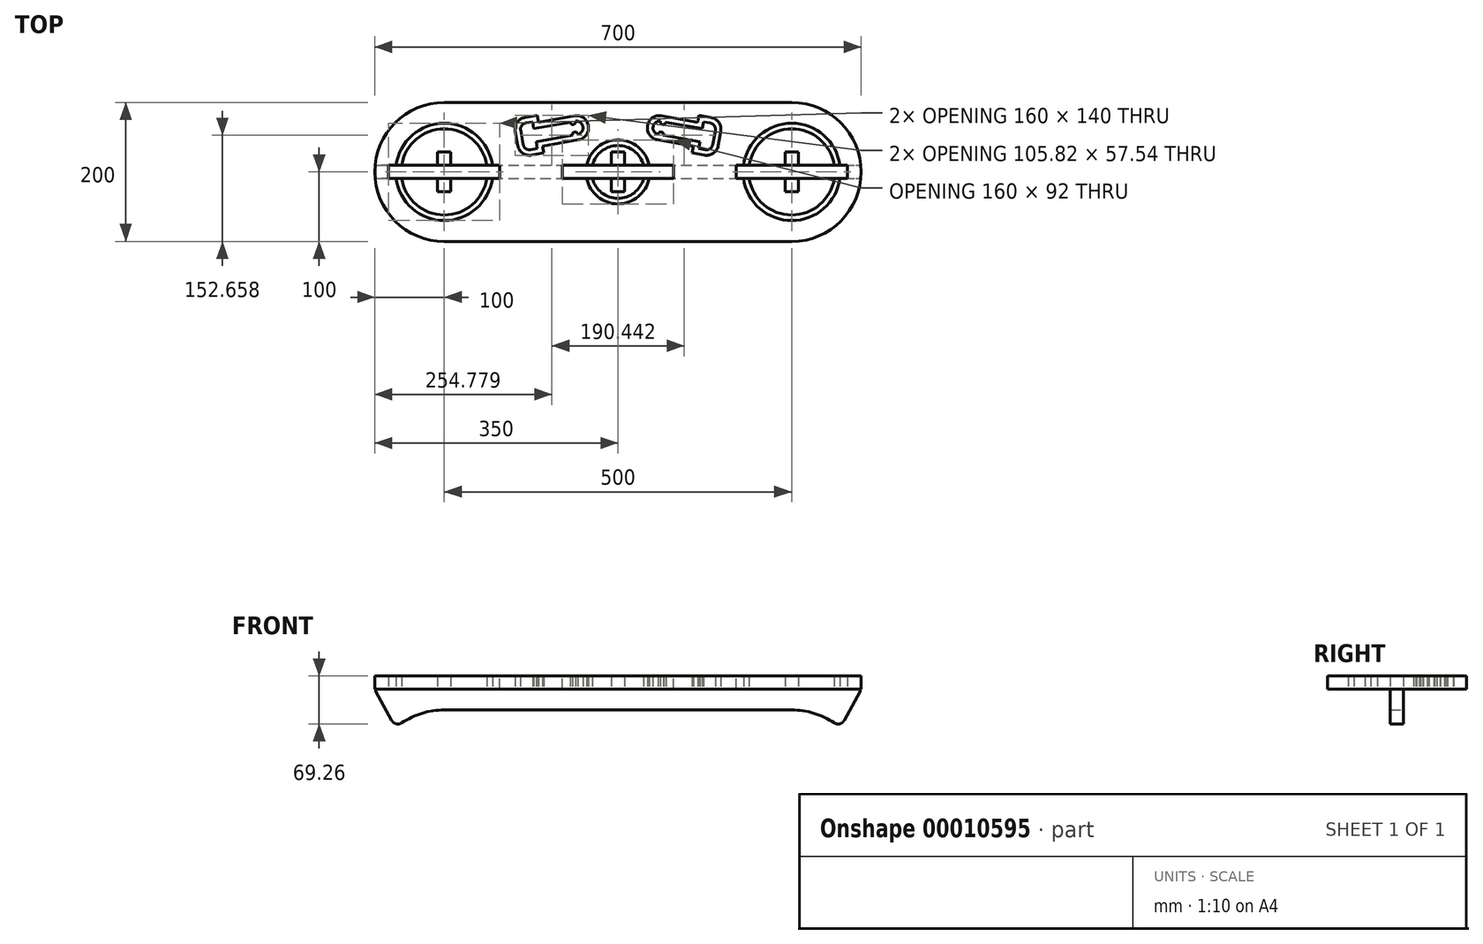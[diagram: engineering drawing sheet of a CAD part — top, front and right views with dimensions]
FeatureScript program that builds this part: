
annotation { "Feature Type Name" : "Feature", "Feature Type Description" : "" }
export const myFeature = defineFeature(function(context is Context, id is Id, definition is map)
    precondition{}
    {
        {
            var Q0;
            Q0=qCreatedBy(makeId("Top.planeOp"),FACE);
            var sketch = newSketch(context, id + "F0", { "sketchPlane" : qUnion([Q0])});
            skLineSegment(sketch, "E0.bottom", {"start": v(-250, 100) * mm, "end": v(250, 100) * mm});
            skLineSegment(sketch, "E0.top", {"start": v(-250, -100) * mm, "end": v(250, -100) * mm});
            skLineSegment(sketch, "E0.left", {"start": v(-250, 100) * mm, "end": v(-250, -100) * mm});
            skLineSegment(sketch, "E0.right", {"start": v(250, 100) * mm, "end": v(250, -100) * mm});
            skLineSegment(sketch, "E1", {"start": v(0, 0) * mm, "end": v(0, 100) * mm, "construction": true});
            skLineSegment(sketch, "E2", {"start": v(250, 0) * mm, "end": v(0, 0) * mm, "construction": true});
            skArc(sketch, "E3", {"start": v(-250, 100) * mm, "mid": v(-350, 0) * mm, "end": v(-250, -100) * mm});
            skArc(sketch, "E4", {"start": v(250, -100) * mm, "mid": v(350, 0) * mm, "end": v(250, 100) * mm});
            skSolve(sketch);
        }
        {
            var Q0;
            Q0=qSketchRegion(id+"F0",true);
            extrude(context, id + "F1", {"entities" : qUnion([Q0]), "depth" : 19 * mm});
        }
        {
            var Q0;
            Q0=qCreatedBy(makeId("Front.planeOp"),FACE);
            var sketch = newSketch(context, id + "F2", { "sketchPlane" : qUnion([Q0])});
            skLineSegment(sketch, "E5.top", {"start": v(-250, -30) * mm, "end": v(0, -30) * mm});
            skLineSegment(sketch, "E6", {"start": v(0, -30) * mm, "end": v(0, 0) * mm, "construction": true});
            skLineSegment(sketch, "E7.top", {"start": v(-330, 19) * mm, "end": v(-170, 19) * mm});
            skLineSegment(sketch, "E7.right", {"start": v(-170, 0) * mm, "end": v(-170, 19) * mm});
            skLineSegment(sketch, "E8.bottom", {"start": v(-80, 0) * mm, "end": v(80, 0) * mm});
            skLineSegment(sketch, "E8.top", {"start": v(-80, 19) * mm, "end": v(80, 19) * mm});
            skLineSegment(sketch, "E8.left", {"start": v(-80, 0) * mm, "end": v(-80, 19) * mm});
            skLineSegment(sketch, "E8.right", {"start": v(80, 0) * mm, "end": v(80, 19) * mm});
            skLineSegment(sketch, "E9", {"start": v(0, 0) * mm, "end": v(0, 19) * mm, "construction": true});
            skLineSegment(sketch, "E10", {"start": v(-320, -55.15) * mm, "end": v(-350, 0) * mm});
            skLineSegment(sketch, "E11.0", {"start": v(-350, 19) * mm, "end": v(-170, 19) * mm, "construction": true});
            skLineSegment(sketch, "E12.trimOffspring", {"start": v(-80, 0) * mm, "end": v(170, 0) * mm});
            skArc(sketch, "E13", {"start": v(-250, -30) * mm, "mid": v(-287.19, -36.48) * mm, "end": v(-320, -55.15) * mm});
            skLineSegment(sketch, "E14", {"start": v(-250, -30) * mm, "end": v(-250, 19) * mm, "construction": true});
            skLineSegment(sketch, "E15.0.MirrorCS", {"start": v(250, -30) * mm, "end": v(0, -30) * mm});
            skArc(sketch, "E16.0.MirrorCS", {"start": v(250, -30) * mm, "mid": v(287.19, -36.48) * mm, "end": v(320, -55.15) * mm});
            skLineSegment(sketch, "E17.0.MirrorCS", {"start": v(320, -55.15) * mm, "end": v(350, 0) * mm});
            skLineSegment(sketch, "E18.0.MirrorCS", {"start": v(350, 0) * mm, "end": v(350, 0) * mm});
            skLineSegment(sketch, "E19.0.MirrorCS", {"start": v(330, 19) * mm, "end": v(170, 19) * mm});
            skLineSegment(sketch, "E20.0.MirrorCS", {"start": v(170, 0) * mm, "end": v(170, 19) * mm});
            skLineSegment(sketch, "E21", {"start": v(-170, 0) * mm, "end": v(-80, 0) * mm});
            skLineSegment(sketch, "E22", {"start": v(-330, 19) * mm, "end": v(-330, 0) * mm});
            skLineSegment(sketch, "E23", {"start": v(-330, 0) * mm, "end": v(-350, 0) * mm});
            skLineSegment(sketch, "E24", {"start": v(-330, 0) * mm, "end": v(-170, 0) * mm});
            skLineSegment(sketch, "E25", {"start": v(-350, 19) * mm, "end": v(-350, 0) * mm, "construction": true});
            skLineSegment(sketch, "E26.0.MirrorCS", {"start": v(330, 0) * mm, "end": v(350, 0) * mm});
            skLineSegment(sketch, "E27.0.MirrorCS", {"start": v(330, 19) * mm, "end": v(330, 0) * mm});
            skLineSegment(sketch, "E28.0.MirrorCS", {"start": v(0, 30) * mm, "end": v(0, 0) * mm, "construction": true});
            skLineSegment(sketch, "E29.0.MirrorCS", {"start": v(330, 0) * mm, "end": v(170, 0) * mm});
            skSolve(sketch);
        }
        {
            var Q0;
            Q0=qSketchRegion(id+"F2",true);
            extrude(context, id + "F3", {"entities" : qUnion([Q0]), "endBound" : BoundingType.SYMMETRIC, "depth" : 19 * mm});
        }
        {
            var Q0;
            Q0=makeQuery(id+"F3.opExtrude","SWEPT_EDGE",EDGE,{"disambiguationData":[OSD([sQuery(id+"F2.wireOp",EDGE,"E10"),sQuery(id+"F2.wireOp",EDGE,"E13")])]});
            var Q1;
            Q1=makeQuery(id+"F3.opExtrude","SWEPT_EDGE",EDGE,{"disambiguationData":[OSD([sQuery(id+"F2.wireOp",EDGE,"E16.0.MirrorCS"),sQuery(id+"F2.wireOp",EDGE,"E17.0.MirrorCS")])]});
            fillet(context, id + "F4", {"entities" : qUnion([Q0, Q1]), "radius" : 10 * mm, "tangentPropagation" : true, "allowEdgeOverflow" : false});
        }
        {
            var Q0;
            Q0=makeQuery(id+"F3.opExtrude","SWEPT_EDGE",EDGE,{"disambiguationData":[OSD([sQuery(id+"F2.wireOp",EDGE,"E10"),sQuery(id+"F2.wireOp",EDGE,"E23")])]});
            var Q1;
            Q1=makeQuery(id+"F3.opExtrude","SWEPT_EDGE",EDGE,{"disambiguationData":[OSD([sQuery(id+"F2.wireOp",EDGE,"E17.0.MirrorCS"),sQuery(id+"F2.wireOp",EDGE,"E26.0.MirrorCS")])]});
            fillet(context, id + "F5", {"entities" : qUnion([Q0, Q1]), "radius" : 2 * mm, "tangentPropagation" : true, "allowEdgeOverflow" : false});
        }
        {
            var Q0;
            Q0=qCreatedBy(makeId("Top.planeOp"),FACE);
            var sketch = newSketch(context, id + "F6", { "sketchPlane" : qUnion([Q0])});
            skCircle(sketch, "E30", {"center": v(-250, 0) * mm, "radius": 70 * mm});
            skCircle(sketch, "E31", {"center": v(250, 0) * mm, "radius": 70 * mm});
            skCircle(sketch, "E32", {"center": v(0, 0) * mm, "radius": 46 * mm});
            skCircle(sketch, "E33", {"center": v(-250, 0) * mm, "radius": 62 * mm});
            skCircle(sketch, "E34", {"center": v(250, 0) * mm, "radius": 62 * mm});
            skCircle(sketch, "E35", {"center": v(0, 0) * mm, "radius": 38 * mm});
            skLineSegment(sketch, "E36", {"start": v(-250, 62) * mm, "end": v(-250, 70) * mm});
            skLineSegment(sketch, "E37", {"start": v(0, 38) * mm, "end": v(0, 46) * mm});
            skLineSegment(sketch, "E38", {"start": v(250, 62) * mm, "end": v(250, 70) * mm});
            skLineSegment(sketch, "E39.bottom", {"start": v(-9.5, 9.5) * mm, "end": v(9.5, 9.5) * mm});
            skLineSegment(sketch, "E39.top", {"start": v(-9.5, 28.5) * mm, "end": v(9.5, 28.5) * mm});
            skLineSegment(sketch, "E39.left", {"start": v(-9.5, 9.5) * mm, "end": v(-9.5, 28.5) * mm});
            skLineSegment(sketch, "E39.right", {"start": v(9.5, 9.5) * mm, "end": v(9.5, 28.5) * mm});
            skLineSegment(sketch, "E40.bottom", {"start": v(9.5, -9.5) * mm, "end": v(-9.5, -9.5) * mm});
            skLineSegment(sketch, "E40.top", {"start": v(9.5, -28.5) * mm, "end": v(-9.5, -28.5) * mm});
            skLineSegment(sketch, "E40.left", {"start": v(9.5, -9.5) * mm, "end": v(9.5, -28.5) * mm});
            skLineSegment(sketch, "E40.right", {"start": v(-9.5, -9.5) * mm, "end": v(-9.5, -28.5) * mm});
            skLineSegment(sketch, "E41", {"start": v(0, 9.5) * mm, "end": v(0, 0) * mm});
            skLineSegment(sketch, "E42", {"start": v(0, 0) * mm, "end": v(0, -9.5) * mm});
            skLineSegment(sketch, "E43.left", {"start": v(-259.5, 9.5) * mm, "end": v(-259.5, 28.5) * mm});
            skLineSegment(sketch, "E43.top", {"start": v(-259.5, 28.5) * mm, "end": v(-240.5, 28.5) * mm});
            skLineSegment(sketch, "E43.right", {"start": v(-240.5, 9.5) * mm, "end": v(-240.5, 28.5) * mm});
            skLineSegment(sketch, "E43.bottom", {"start": v(-259.5, 9.5) * mm, "end": v(-240.5, 9.5) * mm});
            skLineSegment(sketch, "E44", {"start": v(-250, 9.5) * mm, "end": v(-250, 0) * mm});
            skLineSegment(sketch, "E45", {"start": v(-250, 0) * mm, "end": v(-250, -9.5) * mm});
            skLineSegment(sketch, "E46.bottom", {"start": v(-240.5, -9.5) * mm, "end": v(-259.5, -9.5) * mm});
            skLineSegment(sketch, "E46.right", {"start": v(-259.5, -9.5) * mm, "end": v(-259.5, -28.5) * mm});
            skLineSegment(sketch, "E46.top", {"start": v(-240.5, -28.5) * mm, "end": v(-259.5, -28.5) * mm});
            skLineSegment(sketch, "E46.left", {"start": v(-240.5, -9.5) * mm, "end": v(-240.5, -28.5) * mm});
            skLineSegment(sketch, "E47.left", {"start": v(240.5, 9.5) * mm, "end": v(240.5, 28.5) * mm});
            skLineSegment(sketch, "E47.top", {"start": v(240.5, 28.5) * mm, "end": v(259.5, 28.5) * mm});
            skLineSegment(sketch, "E47.right", {"start": v(259.5, 9.5) * mm, "end": v(259.5, 28.5) * mm});
            skLineSegment(sketch, "E47.bottom", {"start": v(240.5, 9.5) * mm, "end": v(259.5, 9.5) * mm});
            skLineSegment(sketch, "E48", {"start": v(250, 9.5) * mm, "end": v(250, 0) * mm});
            skLineSegment(sketch, "E49", {"start": v(250, 0) * mm, "end": v(250, -9.5) * mm});
            skLineSegment(sketch, "E50.bottom", {"start": v(259.5, -9.5) * mm, "end": v(240.5, -9.5) * mm});
            skLineSegment(sketch, "E50.right", {"start": v(240.5, -9.5) * mm, "end": v(240.5, -28.5) * mm});
            skLineSegment(sketch, "E50.top", {"start": v(259.5, -28.5) * mm, "end": v(240.5, -28.5) * mm});
            skLineSegment(sketch, "E50.left", {"start": v(259.5, -9.5) * mm, "end": v(259.5, -28.5) * mm});
            skLineSegment(sketch, "E51", {"start": v(0, -38) * mm, "end": v(249.37, -38) * mm, "construction": true});
            skSolve(sketch);
        }
        {
            var Q0;
            {var subQ3=sQuery(id+"F6.wireOp",EDGE,"E43.left");Q0=makeQuery(id+"F6.imprint","IMPRINT",FACE,{"disambiguationData":[TD([[makeQuery(id+"F6.imprint","IMPRINT",EDGE,{"derivedFrom":subQ3}),-1.0]])]});}
            var Q1;
            {var subQ1=sQuery(id+"F6.wireOp",EDGE,"E46.right");Q1=makeQuery(id+"F6.imprint","IMPRINT",FACE,{"disambiguationData":[TD([[makeQuery(id+"F6.imprint","IMPRINT",EDGE,{"derivedFrom":subQ1}),1.0]])]});}
            var Q2;
            Q2=makeQuery(id+"F6.imprint","IMPRINT",FACE,{"disambiguationData":[TD([[makeQuery(id+"F6.imprint","IMPRINT",EDGE,{"derivedFrom":sQuery(id+"F6.wireOp",EDGE,"E30")}),1.0]])]});
            var Q3;
            Q3=makeQuery(id+"F6.imprint","IMPRINT",FACE,{"disambiguationData":[TD([[makeQuery(id+"F6.imprint","IMPRINT",EDGE,{"derivedFrom":sQuery(id+"F6.wireOp",EDGE,"E32")}),1.0]])]});
            var Q4;
            Q4=makeQuery(id+"F6.imprint","IMPRINT",FACE,{"disambiguationData":[TD([[makeQuery(id+"F6.imprint","IMPRINT",EDGE,{"derivedFrom":sQuery(id+"F6.wireOp",EDGE,"E39.top")}),-1.0]])]});
            var Q5;
            Q5=makeQuery(id+"F6.imprint","IMPRINT",FACE,{"disambiguationData":[TD([[makeQuery(id+"F6.imprint","IMPRINT",EDGE,{"derivedFrom":sQuery(id+"F6.wireOp",EDGE,"E40.top")}),-1.0]])]});
            var Q6;
            Q6=makeQuery(id+"F6.imprint","IMPRINT",FACE,{"disambiguationData":[TD([[makeQuery(id+"F6.imprint","IMPRINT",EDGE,{"derivedFrom":sQuery(id+"F6.wireOp",EDGE,"E31")}),1.0]])]});
            var Q7;
            {var subQ1=sQuery(id+"F6.wireOp",EDGE,"E50.right");Q7=makeQuery(id+"F6.imprint","IMPRINT",FACE,{"disambiguationData":[TD([[makeQuery(id+"F6.imprint","IMPRINT",EDGE,{"derivedFrom":subQ1}),1.0]])]});}
            var Q8;
            {var subQ3=sQuery(id+"F6.wireOp",EDGE,"E47.left");Q8=makeQuery(id+"F6.imprint","IMPRINT",FACE,{"disambiguationData":[TD([[makeQuery(id+"F6.imprint","IMPRINT",EDGE,{"derivedFrom":subQ3}),-1.0]])]});}
            extrude(context, id + "F7", {"entities" : qUnion([Q0, Q1, Q2, Q3, Q4, Q5, Q6, Q7, Q8]), "operationType" : NewBodyOperationType.REMOVE, "endBound" : BoundingType.THROUGH_ALL, "depth" : 25 * mm});
        }
        {
            var Q0;
            Q0=makeQuery(id+"F2.imprint","IMPRINT",FACE,{"disambiguationData":[TD([[makeQuery(id+"F2.imprint","IMPRINT",EDGE,{"derivedFrom":sQuery(id+"F2.wireOp",EDGE,"E7.top")}),-1.0]])]});
            var Q1;
            Q1=makeQuery(id+"F2.imprint","IMPRINT",FACE,{"disambiguationData":[TD([[makeQuery(id+"F2.imprint","IMPRINT",EDGE,{"derivedFrom":sQuery(id+"F2.wireOp",EDGE,"E8.top")}),-1.0]])]});
            var Q2;
            Q2=makeQuery(id+"F2.imprint","IMPRINT",FACE,{"disambiguationData":[TD([[makeQuery(id+"F2.imprint","IMPRINT",EDGE,{"derivedFrom":sQuery(id+"F2.wireOp",EDGE,"E19.0.MirrorCS")}),1.0]])]});
            extrude(context, id + "F8", {"entities" : qUnion([Q0, Q1, Q2]), "operationType" : NewBodyOperationType.REMOVE, "endBound" : BoundingType.SYMMETRIC, "oppositeDirection" : true, "depth" : 19 * mm});
        }
        {
            var Q0;
            Q0=qCreatedBy(makeId("Top.planeOp"),FACE);
            var sketch = newSketch(context, id + "F9", { "sketchPlane" : qUnion([Q0])});
            skLineSegment(sketch, "E52.bottom", {"start": v(-65.62, 52.8) * mm, "end": v(-117.82, 43.6) * mm});
            skLineSegment(sketch, "E52.top", {"start": v(-68.92, 71.52) * mm, "end": v(-121.12, 62.31) * mm});
            skLineSegment(sketch, "E52.left", {"start": v(-65.62, 52.8) * mm, "end": v(-68.92, 71.52) * mm, "construction": true});
            skLineSegment(sketch, "E52.right", {"start": v(-117.82, 43.6) * mm, "end": v(-121.12, 62.31) * mm, "construction": true});
            skLineSegment(sketch, "E53.bottom", {"start": v(-116.08, 33.76) * mm, "end": v(-125.93, 32.02) * mm});
            skLineSegment(sketch, "E53.top", {"start": v(-122.85, 72.16) * mm, "end": v(-132.7, 70.43) * mm});
            skLineSegment(sketch, "E53.right", {"start": v(-136.35, 39.32) * mm, "end": v(-140, 60) * mm});
            skLineSegment(sketch, "E54", {"start": v(-121.12, 62.31) * mm, "end": v(-122.85, 72.16) * mm});
            skLineSegment(sketch, "E55", {"start": v(-117.82, 43.6) * mm, "end": v(-116.08, 33.76) * mm});
            skLineSegment(sketch, "E56.top", {"start": v(-61.04, 72.9) * mm, "end": v(-61.04, 72.9) * mm});
            skLineSegment(sketch, "E56.left", {"start": v(-57.74, 54.2) * mm, "end": v(-61.04, 72.9) * mm, "construction": true});
            skLineSegment(sketch, "E56.right", {"start": v(-50.44, 64.62) * mm, "end": v(-50.62, 65.6) * mm});
            skArc(sketch, "E57", {"start": v(-57.74, 54.2) * mm, "mid": v(-62.38, 57.44) * mm, "end": v(-65.62, 52.8) * mm});
            skArc(sketch, "E58", {"start": v(-68.92, 71.52) * mm, "mid": v(-64.29, 68.27) * mm, "end": v(-61.04, 72.9) * mm});
            skPoint(sketch, "E59.visualSharp", {"position": v(-20.34, -106.1) * mm});
            skArc(sketch, "E59.filletArc", {"start": v(-57.74, 54.2) * mm, "mid": v(-51.93, 57.9) * mm, "end": v(-50.44, 64.62) * mm});
            skPoint(sketch, "E60.visualSharp", {"position": v(-52.18, 74.47) * mm});
            skArc(sketch, "E60.filletArc", {"start": v(-50.62, 65.6) * mm, "mid": v(-54.32, 71.42) * mm, "end": v(-61.04, 72.9) * mm});
            skPoint(sketch, "E61.visualSharp", {"position": v(-134.8, 30.46) * mm});
            skArc(sketch, "E61.filletArc", {"start": v(-136.35, 39.32) * mm, "mid": v(-132.65, 33.5) * mm, "end": v(-125.93, 32.02) * mm});
            skPoint(sketch, "E62.visualSharp", {"position": v(-141.56, 68.86) * mm});
            skArc(sketch, "E62.filletArc", {"start": v(-132.7, 70.43) * mm, "mid": v(-138.5, 66.73) * mm, "end": v(-140, 60) * mm});
            skLineSegment(sketch, "E63", {"start": v(-68.92, 71.52) * mm, "end": v(-61.04, 72.9) * mm, "construction": true});
            skLineSegment(sketch, "E64", {"start": v(-65.62, 52.8) * mm, "end": v(-57.74, 54.2) * mm, "construction": true});
            skLineSegment(sketch, "E65", {"start": v(0, 0) * mm, "end": v(0, 107.47) * mm, "construction": true});
            skLineSegment(sketch, "E66.0.MirrorCS", {"start": v(68.92, 71.52) * mm, "end": v(121.12, 62.31) * mm});
            skLineSegment(sketch, "E67.0.MirrorCS", {"start": v(121.12, 62.31) * mm, "end": v(122.85, 72.16) * mm});
            skLineSegment(sketch, "E68.0.MirrorCS", {"start": v(122.85, 72.16) * mm, "end": v(132.7, 70.43) * mm});
            skPoint(sketch, "E69.0.MirrorP", {"position": v(141.56, 68.86) * mm});
            skArc(sketch, "E70.0.MirrorCS", {"start": v(132.7, 70.43) * mm, "mid": v(138.5, 66.73) * mm, "end": v(140, 60) * mm});
            skLineSegment(sketch, "E71.0.MirrorCS", {"start": v(136.35, 39.32) * mm, "end": v(140, 60) * mm});
            skArc(sketch, "E72.0.MirrorCS", {"start": v(136.35, 39.32) * mm, "mid": v(132.65, 33.5) * mm, "end": v(125.93, 32.02) * mm});
            skLineSegment(sketch, "E73.0.MirrorCS", {"start": v(116.08, 33.76) * mm, "end": v(125.93, 32.02) * mm});
            skLineSegment(sketch, "E74.0.MirrorCS", {"start": v(117.82, 43.6) * mm, "end": v(116.08, 33.76) * mm});
            skLineSegment(sketch, "E75.0.MirrorCS", {"start": v(65.62, 52.8) * mm, "end": v(117.82, 43.6) * mm});
            skArc(sketch, "E76.0.MirrorCS", {"start": v(57.74, 54.2) * mm, "mid": v(62.38, 57.44) * mm, "end": v(65.62, 52.8) * mm});
            skArc(sketch, "E77.0.MirrorCS", {"start": v(57.74, 54.2) * mm, "mid": v(51.93, 57.9) * mm, "end": v(50.44, 64.62) * mm});
            skLineSegment(sketch, "E78.0.MirrorCS", {"start": v(50.44, 64.62) * mm, "end": v(50.62, 65.6) * mm});
            skArc(sketch, "E79.0.MirrorCS", {"start": v(50.62, 65.6) * mm, "mid": v(54.32, 71.42) * mm, "end": v(61.04, 72.9) * mm});
            skArc(sketch, "E80.0.MirrorCS", {"start": v(68.92, 71.52) * mm, "mid": v(64.29, 68.27) * mm, "end": v(61.04, 72.9) * mm});
            skArc(sketch, "E81.0", {"start": v(-144.23, 37.93) * mm, "mid": v(-137.24, 26.96) * mm, "end": v(-124.54, 24.14) * mm});
            skLineSegment(sketch, "E81.1", {"start": v(-106.81, 27.27) * mm, "end": v(-124.54, 24.14) * mm});
            skLineSegment(sketch, "E81.2", {"start": v(-108.55, 37.11) * mm, "end": v(-106.81, 27.27) * mm});
            skLineSegment(sketch, "E81.3", {"start": v(-64.23, 44.93) * mm, "end": v(-108.55, 37.11) * mm});
            skLineSegment(sketch, "E81.4", {"start": v(-64.23, 44.93) * mm, "end": v(-56.35, 46.32) * mm});
            skLineSegment(sketch, "E81.5", {"start": v(-144.23, 37.93) * mm, "end": v(-147.88, 58.61) * mm});
            skArc(sketch, "E81.6", {"start": v(-56.35, 46.32) * mm, "mid": v(-45.38, 53.3) * mm, "end": v(-42.56, 66.01) * mm});
            skLineSegment(sketch, "E81.7", {"start": v(-42.56, 66.01) * mm, "end": v(-42.74, 67) * mm});
            skArc(sketch, "E81.8", {"start": v(-42.74, 67) * mm, "mid": v(-49.73, 77.97) * mm, "end": v(-62.43, 80.79) * mm});
            skLineSegment(sketch, "E81.9", {"start": v(-70.3, 79.4) * mm, "end": v(-62.43, 80.79) * mm});
            skLineSegment(sketch, "E81.10", {"start": v(-70.3, 79.4) * mm, "end": v(-114.63, 71.58) * mm});
            skLineSegment(sketch, "E81.11", {"start": v(-114.63, 71.58) * mm, "end": v(-116.36, 81.43) * mm});
            skLineSegment(sketch, "E81.12", {"start": v(-116.36, 81.43) * mm, "end": v(-134.09, 78.3) * mm});
            skArc(sketch, "E81.13", {"start": v(-134.09, 78.3) * mm, "mid": v(-145.06, 71.31) * mm, "end": v(-147.88, 58.61) * mm});
            skLineSegment(sketch, "E82.0.MirrorCS", {"start": v(144.23, 37.93) * mm, "end": v(147.88, 58.61) * mm});
            skArc(sketch, "E83.0.MirrorCS", {"start": v(144.23, 37.93) * mm, "mid": v(137.24, 26.96) * mm, "end": v(124.54, 24.14) * mm});
            skLineSegment(sketch, "E84.0.MirrorCS", {"start": v(106.81, 27.27) * mm, "end": v(124.54, 24.14) * mm});
            skLineSegment(sketch, "E85.0.MirrorCS", {"start": v(108.55, 37.11) * mm, "end": v(106.81, 27.27) * mm});
            skLineSegment(sketch, "E86.0.MirrorCS", {"start": v(64.23, 44.93) * mm, "end": v(108.55, 37.11) * mm});
            skLineSegment(sketch, "E87.0.MirrorCS", {"start": v(64.23, 44.93) * mm, "end": v(56.35, 46.32) * mm});
            skArc(sketch, "E88.0.MirrorCS", {"start": v(56.35, 46.32) * mm, "mid": v(45.38, 53.3) * mm, "end": v(42.56, 66.01) * mm});
            skLineSegment(sketch, "E89.0.MirrorCS", {"start": v(42.56, 66.01) * mm, "end": v(42.74, 67) * mm});
            skArc(sketch, "E90.0.MirrorCS", {"start": v(42.74, 67) * mm, "mid": v(49.73, 77.97) * mm, "end": v(62.43, 80.79) * mm});
            skLineSegment(sketch, "E91.0.MirrorCS", {"start": v(70.3, 79.4) * mm, "end": v(62.43, 80.79) * mm});
            skLineSegment(sketch, "E92.0.MirrorCS", {"start": v(70.3, 79.4) * mm, "end": v(114.63, 71.58) * mm});
            skLineSegment(sketch, "E93.0.MirrorCS", {"start": v(114.63, 71.58) * mm, "end": v(116.36, 81.43) * mm});
            skLineSegment(sketch, "E94.0.MirrorCS", {"start": v(116.36, 81.43) * mm, "end": v(134.09, 78.3) * mm});
            skArc(sketch, "E95.0.MirrorCS", {"start": v(134.09, 78.3) * mm, "mid": v(145.06, 71.31) * mm, "end": v(147.88, 58.61) * mm});
            skSolve(sketch);
        }
        {
            var Q0;
            Q0=makeQuery(id+"F9.imprint","IMPRINT",FACE,{"disambiguationData":[TD([[makeQuery(id+"F9.imprint","IMPRINT",EDGE,{"derivedFrom":sQuery(id+"F9.wireOp",EDGE,"E52.bottom")}),1.0]])]});
            var Q1;
            Q1=makeQuery(id+"F9.imprint","IMPRINT",FACE,{"disambiguationData":[TD([[makeQuery(id+"F9.imprint","IMPRINT",EDGE,{"derivedFrom":sQuery(id+"F9.wireOp",EDGE,"E66.0.MirrorCS")}),1.0]])]});
            extrude(context, id + "F10", {"entities" : qUnion([Q0, Q1]), "operationType" : NewBodyOperationType.REMOVE, "endBound" : BoundingType.THROUGH_ALL, "depth" : 25 * mm});
        }
    });
